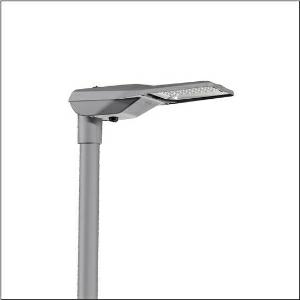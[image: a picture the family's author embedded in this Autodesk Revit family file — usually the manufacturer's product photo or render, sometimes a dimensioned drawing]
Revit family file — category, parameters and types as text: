
# Revit family: streetlight_sl_21_iq_mini___st0_5a_5xe2b31y08gb_b50d
name_source: partatom
category: Lighting Fixtures
units: mm (PartAtom-declared; Revit-internal decimal feet)

## family parameters
Cut with Voids When Loaded = No
Host = Face
Light Source = No
Part Type = Normal
Room Calculation Point = No
Round Connector Dimension = Use Diameter
Shared = No

## types (1)
- --- (1 x LED, 5990 lm, 39.8 W, 3000K)
    Apparent Load = 40 VA
    CIE Flux Codes = 41 75 97 100 100
    Color Rendering = 70
    Color Temperature = 3000K
    Default Elevation = 1800 mm
    Description = Streetlight SL 21 iQ mini, mast luminaire, primary light control with lens, of PMMA, primary optical cover: cover, of toughened safety glass, transparent, light distribution: ST0.5a, light emission: direct distribution, primary light characteristic: asymmetric, installation type: post-top, side-entry, LED, High Power LED, rated luminous flux: 5.990lm, luminous efficacy: 151lm/W, light colour: 730, colour temperature: 3000K, control gear: iQ-Street Remote, D4i with power reduction, control: pre-setting: logarithmic dimming characteristic, Street-Remote, Auto-Match, Temp-Guard, Lumen-Switch, Night-Set, Smart-Wire, Light-Fading, Desk-Remote (wireless, voltage-free reading and setting of iQ features in the workshop via application-optimized NFC function/RFID function), optimised constant luminous flux control (CLO 2.0), mains connection: 220..240V, AC, 50/60Hz, start of lifetime: 40W, end of service life: 41W, reduction: 18W, luminaire housing, of diecast aluminium, powder-coated, Siteco® metallic grey (DB 702S), corrosivity category C5 mid according to DIN EN ISO 12944, please order mast flange separately, inclination adjustable: 0°, 5°, 10°, 15°, sealing non-destructively replaceable, multi-level sealing system, length: 628mm, width: 235mm, height: 110mm, mast flange for spigot size: 42mm (side-entry): 5XC10008XM4, 60/48mm (side-entry/post-top): 5XC10108XM2, 76/60mm (side-entry/post-top): 5XC10108XM1, mounting height: 4..8m, Smart Interface below and above, protection rating (complete): IP66, insulation class (complete): insulation class II (safety insulation), certification: CE, ENEC, ENEC+, VDE, impact resistance: IK10, permissible operating ambient temperature for outdoor applications: -40..+50°C, standard-compliant lighting for roads and squares, packaging unit: 1 piece

Light Distribution: ST0.5a
    Height = 110 mm
    Lamp = 1 x LED
    Lamp Light Flux = 5990 lm
    Lamp Power = 39.8 W
    Lamp count = 1
    Length = 625 mm
    Luminous efficacy = 151 lm/W
    Manufacturer = Siteco
    ModVariant = No
    Model = 5XE2B31Y08GB
    Number of Poles = 1
    OnlyDefault = Yes
    Power Factor = 1
    Product Name = Streetlight SL 21 iQ mini | ST0.5a
    Product group = mast luminaire | pylon top
    ProductGroupID = 6100
    Protection Class = Protection class II
    Protection Degree = IP 66
    RLX_Detail_Level = 1
    RLX_Emergency_Light_Flux = 0 lm
    RLX_Emergency_Type = 0
    RLX_Emergency_Type_DB = No
    RlxData = <blob elided: 37745 chars, md5=66790dc7>
    Socket = socket
    Standby Power = 0 W
    System Light Flux = 5990 lm
    System Power = 40 W
    Type Comments = factory setting: luminous flux: 100 % | dim-lin: 254 | 800 mA
    Type Image = l_1003514.jpg
    URL = http://relux.com
    VarID = @adj_116142
    Voltage = 0 V
    Weight = 0.00 kg
    Width = 234 mm

## geometry (parser evidence)
native form markers: Blend x4, Sweep x11
no freeform markers — native parametric forms only
